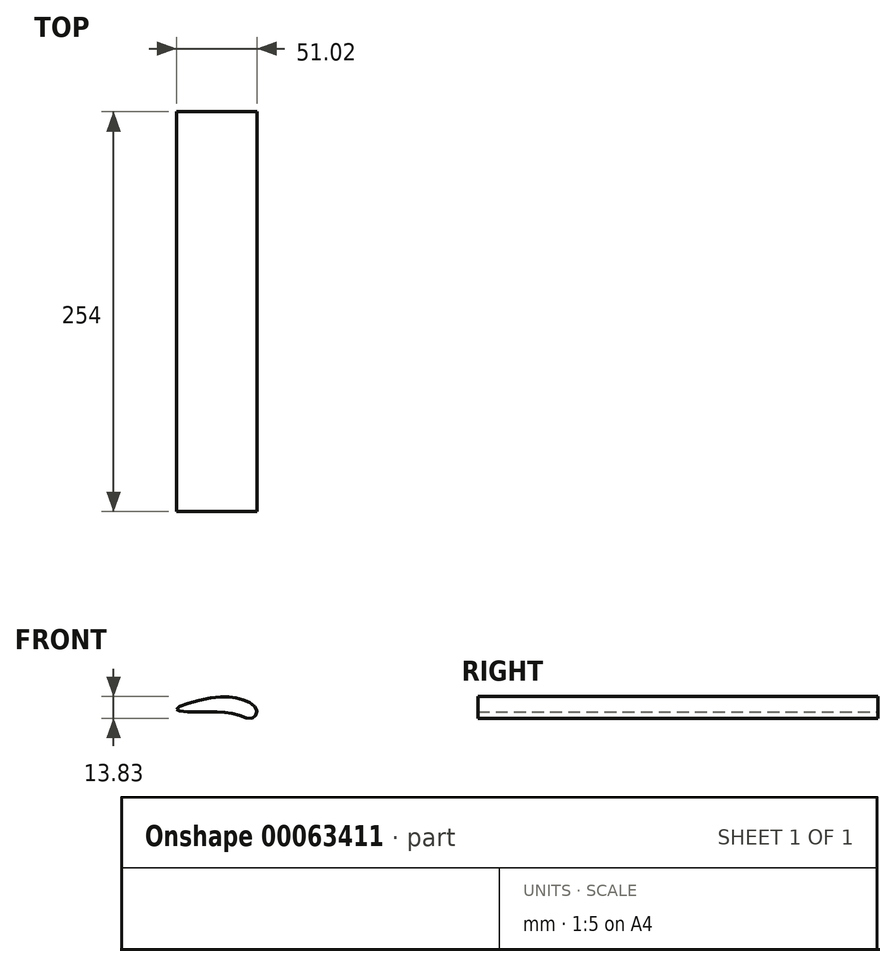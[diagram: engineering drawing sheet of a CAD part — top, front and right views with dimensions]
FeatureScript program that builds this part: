
annotation { "Feature Type Name" : "Feature", "Feature Type Description" : "" }
export const myFeature = defineFeature(function(context is Context, id is Id, definition is map)
    precondition{}
    {
        {
            var Q0;
            Q0=qCreatedBy(makeId("Front.planeOp"),FACE);
            var sketch = newSketch(context, id + "F0", { "sketchPlane" : qUnion([Q0])});
            skFitSpline(sketch, "E0", {"points": [v(0, 0) * mm, v(22.75, 7.4) * mm, v(41.52, 6.3) * mm, v(50.8, 0) * mm, v(48.6, -5.41) * mm, v(36.66, -2.98) * mm, v(17, -1.66) * mm, v(0, 0) * mm]});
            skSolve(sketch);
        }
        {
            var Q0;
            Q0=qSketchRegion(id+"F0",true);
            extrude(context, id + "F1", {"entities" : qUnion([Q0]), "depth" : 254 * mm});
        }
    });
